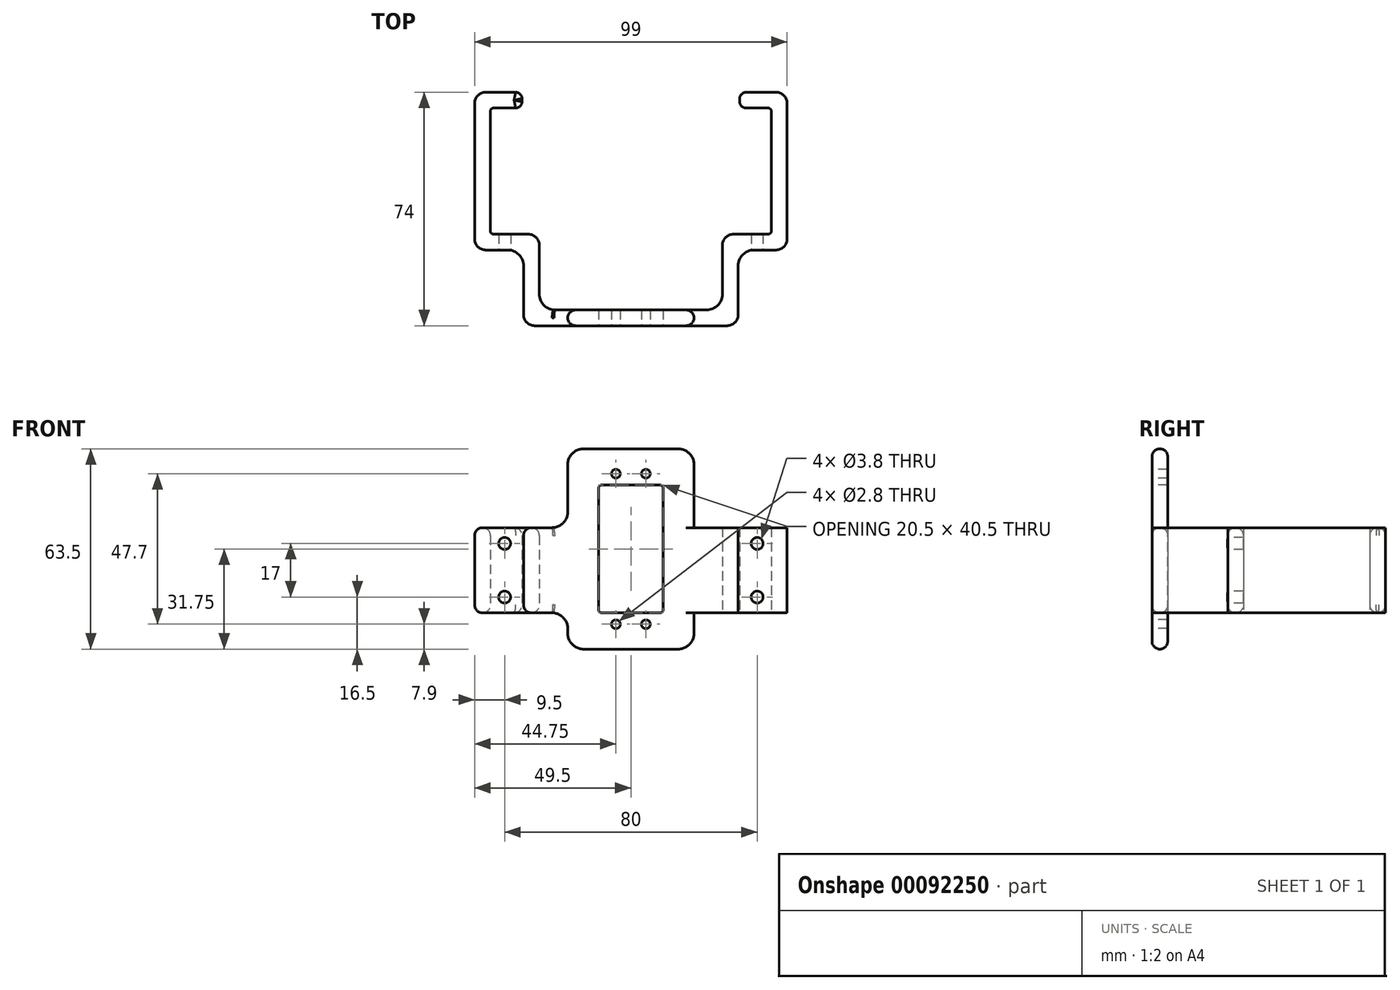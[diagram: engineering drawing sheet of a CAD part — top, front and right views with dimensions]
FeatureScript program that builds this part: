
annotation { "Feature Type Name" : "Feature", "Feature Type Description" : "" }
export const myFeature = defineFeature(function(context is Context, id is Id, definition is map)
    precondition{}
    {
        {
            var Q0;
            Q0=qCreatedBy(makeId("Top.planeOp"),FACE);
            var sketch = newSketch(context, id + "F0", { "sketchPlane" : qUnion([Q0])});
            skLineSegment(sketch, "E0.bottom", {"start": v(-44.5, -20) * mm, "end": v(44.5, -20) * mm, "construction": true});
            skLineSegment(sketch, "E0.top", {"start": v(-44.5, 20) * mm, "end": v(44.5, 20) * mm, "construction": true});
            skLineSegment(sketch, "E0.left", {"start": v(-44.5, -20) * mm, "end": v(-44.5, 20) * mm, "construction": true});
            skLineSegment(sketch, "E0.right", {"start": v(44.5, -20) * mm, "end": v(44.5, 20) * mm, "construction": true});
            skPoint(sketch, "E0.middle", {"position": v(0, 0) * mm});
            skLineSegment(sketch, "E1", {"start": v(-10.3, -35.5) * mm, "end": v(9.7, -35.5) * mm, "construction": true});
            skLineSegment(sketch, "E2", {"start": v(-44.5, 20) * mm, "end": v(-34.5, 20) * mm});
            skLineSegment(sketch, "E3", {"start": v(-34.5, 20) * mm, "end": v(-34.5, 25) * mm});
            skLineSegment(sketch, "E4", {"start": v(-34.5, 25) * mm, "end": v(-49.5, 25) * mm});
            skLineSegment(sketch, "E5", {"start": v(-49.5, 25) * mm, "end": v(-49.5, -25) * mm});
            skLineSegment(sketch, "E6", {"start": v(-49.5, -25) * mm, "end": v(-34, -25) * mm});
            skLineSegment(sketch, "E7", {"start": v(-34, -25) * mm, "end": v(-34, -49) * mm});
            skLineSegment(sketch, "E8", {"start": v(-34, -49) * mm, "end": v(0, -49) * mm});
            skLineSegment(sketch, "E9", {"start": v(-44.5, 20) * mm, "end": v(-44.5, -20) * mm});
            skLineSegment(sketch, "E10", {"start": v(-29, -20) * mm, "end": v(-29, -44) * mm});
            skLineSegment(sketch, "E11", {"start": v(-29, -44) * mm, "end": v(0, -44) * mm});
            skLineSegment(sketch, "E12", {"start": v(-29, -20) * mm, "end": v(-44.5, -20) * mm});
            skLineSegment(sketch, "E13.MirrorCS", {"start": v(29, -44) * mm, "end": v(0, -44) * mm});
            skLineSegment(sketch, "E14.MirrorCS", {"start": v(34, -49) * mm, "end": v(0, -49) * mm});
            skLineSegment(sketch, "E15.MirrorCS", {"start": v(34, -25) * mm, "end": v(34, -49) * mm});
            skLineSegment(sketch, "E16.MirrorCS", {"start": v(49.5, -25) * mm, "end": v(34, -25) * mm});
            skLineSegment(sketch, "E17.MirrorCS", {"start": v(49.5, 25) * mm, "end": v(49.5, -25) * mm});
            skLineSegment(sketch, "E18.MirrorCS", {"start": v(34.5, 25) * mm, "end": v(49.5, 25) * mm});
            skLineSegment(sketch, "E19.MirrorCS", {"start": v(34.5, 20) * mm, "end": v(34.5, 25) * mm});
            skLineSegment(sketch, "E20.MirrorCS", {"start": v(44.5, 20) * mm, "end": v(34.5, 20) * mm});
            skLineSegment(sketch, "E21.MirrorCS", {"start": v(44.5, 20) * mm, "end": v(44.5, -20) * mm});
            skLineSegment(sketch, "E22.MirrorCS", {"start": v(29, -20) * mm, "end": v(29, -44) * mm});
            skLineSegment(sketch, "E23.MirrorCS", {"start": v(29, -20) * mm, "end": v(44.5, -20) * mm});
            skSolve(sketch);
        }
        {
            var Q0;
            Q0 = qSketchRegion(id + "F0", true);
            extrude(context, id + "F1", {"entities" : qUnion([Q0]), "depth" : 27 * mm});
        }
        {
            var Q0;
            Q0=makeQuery(id+"F1.opExtrude","CAP_FACE",FACE,{"disambiguationData":[OSD([sQuery(id+"F0.wireOp",EDGE,"E2"),sQuery(id+"F0.wireOp",EDGE,"E3"),sQuery(id+"F0.wireOp",EDGE,"E4"),sQuery(id+"F0.wireOp",EDGE,"E5"),sQuery(id+"F0.wireOp",EDGE,"E6"),sQuery(id+"F0.wireOp",EDGE,"E7"),sQuery(id+"F0.wireOp",EDGE,"E8"),sQuery(id+"F0.wireOp",EDGE,"E9"),sQuery(id+"F0.wireOp",EDGE,"E10"),sQuery(id+"F0.wireOp",EDGE,"E11"),sQuery(id+"F0.wireOp",EDGE,"E12"),sQuery(id+"F0.wireOp",EDGE,"E13.MirrorCS"),sQuery(id+"F0.wireOp",EDGE,"E14.MirrorCS"),sQuery(id+"F0.wireOp",EDGE,"E15.MirrorCS"),sQuery(id+"F0.wireOp",EDGE,"E16.MirrorCS"),sQuery(id+"F0.wireOp",EDGE,"E17.MirrorCS"),sQuery(id+"F0.wireOp",EDGE,"E18.MirrorCS"),sQuery(id+"F0.wireOp",EDGE,"E19.MirrorCS"),sQuery(id+"F0.wireOp",EDGE,"E20.MirrorCS"),sQuery(id+"F0.wireOp",EDGE,"E21.MirrorCS"),sQuery(id+"F0.wireOp",EDGE,"E22.MirrorCS"),sQuery(id+"F0.wireOp",EDGE,"E23.MirrorCS")])],"isStart":true});
            var sketch = newSketch(context, id + "F2", { "sketchPlane" : qUnion([Q0])});
            skLineSegment(sketch, "E24.bottom", {"start": v(-20, 49) * mm, "end": v(20, 49) * mm});
            skLineSegment(sketch, "E24.top", {"start": v(-20, 44) * mm, "end": v(20, 44) * mm});
            skLineSegment(sketch, "E24.left", {"start": v(-20, 49) * mm, "end": v(-20, 44) * mm});
            skLineSegment(sketch, "E24.right", {"start": v(20, 49) * mm, "end": v(20, 44) * mm});
            skPoint(sketch, "E24.middle", {"position": v(0, 46.5) * mm});
            skSolve(sketch);
        }
        {
            var Q0;
            Q0 = qSketchRegion(id + "F2", true);
            extrude(context, id + "F3", {"entities" : qUnion([Q0]), "operationType" : NewBodyOperationType.ADD, "depth" : 11.5 * mm});
        }
        {
            var Q0;
            Q0=makeQuery(id+"F1.opExtrude","CAP_FACE",FACE,{"disambiguationData":[OSD([sQuery(id+"F0.wireOp",EDGE,"E2"),sQuery(id+"F0.wireOp",EDGE,"E3"),sQuery(id+"F0.wireOp",EDGE,"E4"),sQuery(id+"F0.wireOp",EDGE,"E5"),sQuery(id+"F0.wireOp",EDGE,"E6"),sQuery(id+"F0.wireOp",EDGE,"E7"),sQuery(id+"F0.wireOp",EDGE,"E8"),sQuery(id+"F0.wireOp",EDGE,"E9"),sQuery(id+"F0.wireOp",EDGE,"E10"),sQuery(id+"F0.wireOp",EDGE,"E11"),sQuery(id+"F0.wireOp",EDGE,"E12"),sQuery(id+"F0.wireOp",EDGE,"E13.MirrorCS"),sQuery(id+"F0.wireOp",EDGE,"E14.MirrorCS"),sQuery(id+"F0.wireOp",EDGE,"E15.MirrorCS"),sQuery(id+"F0.wireOp",EDGE,"E16.MirrorCS"),sQuery(id+"F0.wireOp",EDGE,"E17.MirrorCS"),sQuery(id+"F0.wireOp",EDGE,"E18.MirrorCS"),sQuery(id+"F0.wireOp",EDGE,"E19.MirrorCS"),sQuery(id+"F0.wireOp",EDGE,"E20.MirrorCS"),sQuery(id+"F0.wireOp",EDGE,"E21.MirrorCS"),sQuery(id+"F0.wireOp",EDGE,"E22.MirrorCS"),sQuery(id+"F0.wireOp",EDGE,"E23.MirrorCS")])],"isStart":false});
            var sketch = newSketch(context, id + "F4", { "sketchPlane" : qUnion([Q0])});
            skLineSegment(sketch, "E25.bottom", {"start": v(-20, -49) * mm, "end": v(20, -49) * mm});
            skLineSegment(sketch, "E25.top", {"start": v(-20, -44) * mm, "end": v(20, -44) * mm});
            skLineSegment(sketch, "E25.left", {"start": v(-20, -49) * mm, "end": v(-20, -44) * mm});
            skLineSegment(sketch, "E25.right", {"start": v(20, -49) * mm, "end": v(20, -44) * mm});
            skPoint(sketch, "E25.middle", {"position": v(0, -46.5) * mm});
            skPoint(sketch, "E25.middle.positionSnap0", {"position": v(0, -49) * mm});
            skPoint(sketch, "E25.centerSnap0", {"position": v(0, -49) * mm});
            skSolve(sketch);
        }
        {
            var Q0;
            Q0 = qSketchRegion(id + "F4", true);
            extrude(context, id + "F5", {"entities" : qUnion([Q0]), "operationType" : NewBodyOperationType.ADD, "depth" : 25 * mm});
        }
        {
            var Q0;
            Q0=makeQuery(id+"F5.boolean.opBoolean","MERGE",FACE,{"derivedFrom":[makeQuery(id+"F3.boolean.opBoolean","MERGE",FACE,{"derivedFrom":[makeQuery(id+"F1.opExtrude","SWEPT_FACE",FACE,{"disambiguationData":[OSD([sQuery(id+"F0.wireOp",EDGE,"E8"),sQuery(id+"F0.wireOp",EDGE,"E14.MirrorCS")])]}),makeQuery(id+"F3.opExtrude","SWEPT_FACE",FACE,{"disambiguationData":[OSD([sQuery(id+"F2.wireOp",EDGE,"E24.bottom")])]})]}),makeQuery(id+"F5.opExtrude","SWEPT_FACE",FACE,{"disambiguationData":[OSD([sQuery(id+"F4.wireOp",EDGE,"E25.bottom")])]})]});
            var sketch = newSketch(context, id + "F6", { "sketchPlane" : qUnion([Q0])});
            skLineSegment(sketch, "E26.bottom", {"start": v(-10.25, 0) * mm, "end": v(10.25, 0) * mm});
            skLineSegment(sketch, "E26.top", {"start": v(-10.25, 40.5) * mm, "end": v(10.25, 40.5) * mm});
            skLineSegment(sketch, "E26.left", {"start": v(-10.25, 0) * mm, "end": v(-10.25, 40.5) * mm});
            skLineSegment(sketch, "E26.right", {"start": v(10.25, 0) * mm, "end": v(10.25, 40.5) * mm});
            skPoint(sketch, "E26.middle", {"position": v(0, 20.25) * mm});
            skSolve(sketch);
        }
        {
            var Q0;
            Q0 = qSketchRegion(id + "F6", true);
            extrude(context, id + "F7", {"entities" : qUnion([Q0]), "operationType" : NewBodyOperationType.REMOVE, "oppositeDirection" : true, "depth" : 25 * mm});
        }
        {
            var Q0;
            Q0=makeQuery(id+"F1.opExtrude","SWEPT_EDGE",EDGE,{"disambiguationData":[OSD([sQuery(id+"F0.wireOp",EDGE,"E6"),sQuery(id+"F0.wireOp",EDGE,"E7")])]});
            var Q1;
            Q1=makeQuery(id+"F1.opExtrude","SWEPT_EDGE",EDGE,{"disambiguationData":[OSD([sQuery(id+"F0.wireOp",EDGE,"E15.MirrorCS"),sQuery(id+"F0.wireOp",EDGE,"E16.MirrorCS")])]});
            fillet(context, id + "F8", {"entities" : qUnion([Q0, Q1]), "radius" : 5 * mm, "tangentPropagation" : true, "allowEdgeOverflow" : false});
        }
        {
            var Q0;
            Q0=makeQuery(id+"F1.opExtrude","SWEPT_EDGE",EDGE,{"disambiguationData":[OSD([sQuery(id+"F0.wireOp",EDGE,"E10"),sQuery(id+"F0.wireOp",EDGE,"E12")])]});
            var Q1;
            Q1=makeQuery(id+"F1.opExtrude","SWEPT_EDGE",EDGE,{"disambiguationData":[OSD([sQuery(id+"F0.wireOp",EDGE,"E22.MirrorCS"),sQuery(id+"F0.wireOp",EDGE,"E23.MirrorCS")])]});
            var Q2;
            Q2=makeQuery(id+"F1.opExtrude","SWEPT_EDGE",EDGE,{"disambiguationData":[OSD([sQuery(id+"F0.wireOp",EDGE,"E5"),sQuery(id+"F0.wireOp",EDGE,"E6")])]});
            var Q3;
            Q3=makeQuery(id+"F1.opExtrude","SWEPT_EDGE",EDGE,{"disambiguationData":[OSD([sQuery(id+"F0.wireOp",EDGE,"E7"),sQuery(id+"F0.wireOp",EDGE,"E8")])]});
            var Q4;
            Q4=makeQuery(id+"F1.opExtrude","SWEPT_EDGE",EDGE,{"disambiguationData":[OSD([sQuery(id+"F0.wireOp",EDGE,"E14.MirrorCS"),sQuery(id+"F0.wireOp",EDGE,"E15.MirrorCS")])]});
            var Q5;
            Q5=makeQuery(id+"F1.opExtrude","SWEPT_EDGE",EDGE,{"disambiguationData":[OSD([sQuery(id+"F0.wireOp",EDGE,"E16.MirrorCS"),sQuery(id+"F0.wireOp",EDGE,"E17.MirrorCS")])]});
            var Q6;
            Q6=makeQuery(id+"F1.opExtrude","SWEPT_EDGE",EDGE,{"disambiguationData":[OSD([sQuery(id+"F0.wireOp",EDGE,"E4"),sQuery(id+"F0.wireOp",EDGE,"E5")])]});
            var Q7;
            Q7=makeQuery(id+"F1.opExtrude","SWEPT_EDGE",EDGE,{"disambiguationData":[OSD([sQuery(id+"F0.wireOp",EDGE,"E17.MirrorCS"),sQuery(id+"F0.wireOp",EDGE,"E18.MirrorCS")])]});
            fillet(context, id + "F9", {"entities" : qUnion([Q0, Q1, Q2, Q3, Q4, Q5, Q6, Q7]), "radius" : 3.5 * mm, "tangentPropagation" : true, "allowEdgeOverflow" : false});
        }
        {
            var Q0;
            Q0=makeQuery(id+"F1.opExtrude","SWEPT_EDGE",EDGE,{"disambiguationData":[OSD([sQuery(id+"F0.wireOp",EDGE,"E10"),sQuery(id+"F0.wireOp",EDGE,"E11")])]});
            var Q1;
            Q1=makeQuery(id+"F1.opExtrude","SWEPT_EDGE",EDGE,{"disambiguationData":[OSD([sQuery(id+"F0.wireOp",EDGE,"E13.MirrorCS"),sQuery(id+"F0.wireOp",EDGE,"E22.MirrorCS")])]});
            fillet(context, id + "F10", {"entities" : qUnion([Q0, Q1]), "radius" : 5 * mm, "tangentPropagation" : true, "allowEdgeOverflow" : false});
        }
        {
            var Q0;
            Q0=makeQuery(id+"F3.opExtrude","CAP_EDGE",EDGE,{"disambiguationData":[OSD([sQuery(id+"F2.wireOp",EDGE,"E24.left")])],"isStart":true});
            var Q1;
            Q1=makeQuery(id+"F3.opExtrude","CAP_EDGE",EDGE,{"disambiguationData":[OSD([sQuery(id+"F2.wireOp",EDGE,"E24.right")])],"isStart":true});
            var Q2;
            Q2=makeQuery(id+"F3.opExtrude","CAP_EDGE",EDGE,{"disambiguationData":[OSD([sQuery(id+"F2.wireOp",EDGE,"E24.right")])],"isStart":false});
            var Q3;
            Q3=makeQuery(id+"F3.opExtrude","CAP_EDGE",EDGE,{"disambiguationData":[OSD([sQuery(id+"F2.wireOp",EDGE,"E24.left")])],"isStart":false});
            var Q4;
            Q4=makeQuery(id+"F5.opExtrude","CAP_EDGE",EDGE,{"disambiguationData":[OSD([sQuery(id+"F4.wireOp",EDGE,"E25.left")])],"isStart":false});
            var Q5;
            Q5=makeQuery(id+"F5.opExtrude","CAP_EDGE",EDGE,{"disambiguationData":[OSD([sQuery(id+"F4.wireOp",EDGE,"E25.right")])],"isStart":false});
            var Q6;
            Q6=makeQuery(id+"F5.opExtrude","CAP_EDGE",EDGE,{"disambiguationData":[OSD([sQuery(id+"F4.wireOp",EDGE,"E25.right")])],"isStart":true});
            var Q7;
            Q7=makeQuery(id+"F5.opExtrude","CAP_EDGE",EDGE,{"disambiguationData":[OSD([sQuery(id+"F4.wireOp",EDGE,"E25.left")])],"isStart":true});
            fillet(context, id + "F11", {"entities" : qUnion([Q0, Q1, Q2, Q3, Q4, Q5, Q6, Q7]), "radius" : 5 * mm, "tangentPropagation" : true, "allowEdgeOverflow" : false});
        }
        {
            var Q0;
            Q0=makeQuery(id+"F1.opExtrude","SWEPT_EDGE",EDGE,{"disambiguationData":[OSD([sQuery(id+"F0.wireOp",EDGE,"E2"),sQuery(id+"F0.wireOp",EDGE,"E3")])]});
            var Q1;
            Q1=makeQuery(id+"F1.opExtrude","SWEPT_EDGE",EDGE,{"disambiguationData":[OSD([sQuery(id+"F0.wireOp",EDGE,"E18.MirrorCS"),sQuery(id+"F0.wireOp",EDGE,"E19.MirrorCS")])]});
            var Q2;
            Q2=makeQuery(id+"F1.opExtrude","SWEPT_EDGE",EDGE,{"disambiguationData":[OSD([sQuery(id+"F0.wireOp",EDGE,"E19.MirrorCS"),sQuery(id+"F0.wireOp",EDGE,"E20.MirrorCS")])]});
            var Q3;
            Q3=makeQuery(id+"F1.opExtrude","SWEPT_EDGE",EDGE,{"disambiguationData":[OSD([sQuery(id+"F0.wireOp",EDGE,"E3"),sQuery(id+"F0.wireOp",EDGE,"E4")])]});
            fillet(context, id + "F12", {"entities" : qUnion([Q0, Q1, Q2, Q3]), "radius" : 2 * mm, "tangentPropagation" : true, "allowEdgeOverflow" : false});
        }
        {
            var Q0;
            Q0=makeQuery(id+"F1.opExtrude","SWEPT_EDGE",EDGE,{"disambiguationData":[OSD([sQuery(id+"F0.wireOp",EDGE,"E21.MirrorCS"),sQuery(id+"F0.wireOp",EDGE,"E23.MirrorCS")])]});
            var Q1;
            Q1=makeQuery(id+"F1.opExtrude","SWEPT_EDGE",EDGE,{"disambiguationData":[OSD([sQuery(id+"F0.wireOp",EDGE,"E20.MirrorCS"),sQuery(id+"F0.wireOp",EDGE,"E21.MirrorCS")])]});
            var Q2;
            Q2=makeQuery(id+"F1.opExtrude","SWEPT_EDGE",EDGE,{"disambiguationData":[OSD([sQuery(id+"F0.wireOp",EDGE,"E2"),sQuery(id+"F0.wireOp",EDGE,"E9")])]});
            var Q3;
            Q3=makeQuery(id+"F1.opExtrude","SWEPT_EDGE",EDGE,{"disambiguationData":[OSD([sQuery(id+"F0.wireOp",EDGE,"E9"),sQuery(id+"F0.wireOp",EDGE,"E12")])]});
            fillet(context, id + "F13", {"entities" : qUnion([Q0, Q1, Q2, Q3]), "radius" : 1 * mm, "tangentPropagation" : true, "allowEdgeOverflow" : false});
        }
        {
            var Q0;
            Q0=makeQuery(id+"F1.opExtrude","SWEPT_FACE",FACE,{"disambiguationData":[OSD([sQuery(id+"F0.wireOp",EDGE,"E6")])]});
            var sketch = newSketch(context, id + "F14", { "sketchPlane" : qUnion([Q0])});
            skCircle(sketch, "E27", {"center": v(-40, 22) * mm, "radius": 1.9 * mm});
            skCircle(sketch, "E28", {"center": v(-40, 5) * mm, "radius": 1.9 * mm});
            skLineSegment(sketch, "E29", {"start": v(-40, 27) * mm, "end": v(-40, 0) * mm, "construction": true});
            skCircle(sketch, "E30.MirrorC", {"center": v(40, 5) * mm, "radius": 1.9 * mm});
            skCircle(sketch, "E31.MirrorC", {"center": v(40, 22) * mm, "radius": 1.9 * mm});
            skSolve(sketch);
        }
        {
            var Q0;
            Q0 = qSketchRegion(id + "F14", true);
            extrude(context, id + "F15", {"entities" : qUnion([Q0]), "operationType" : NewBodyOperationType.REMOVE, "oppositeDirection" : true, "depth" : 25 * mm, "hasSecondDirection" : true, "secondDirectionOppositeDirection" : false, "secondDirectionDepth" : 25 * mm});
        }
        {
            var Q0;
            Q0=makeQuery(id+"F7.boolean.opBoolean","COPY",EDGE,{"derivedFrom":makeQuery(id+"F7.opExtrude","SWEPT_EDGE",EDGE,{"disambiguationData":[OSD([sQuery(id+"F6.wireOp",EDGE,"E26.top"),sQuery(id+"F6.wireOp",EDGE,"E26.left")])]})});
            var Q1;
            Q1=makeQuery(id+"F7.boolean.opBoolean","COPY",EDGE,{"derivedFrom":makeQuery(id+"F7.opExtrude","SWEPT_EDGE",EDGE,{"disambiguationData":[OSD([sQuery(id+"F6.wireOp",EDGE,"E26.bottom"),sQuery(id+"F6.wireOp",EDGE,"E26.right")])]})});
            var Q2;
            Q2=makeQuery(id+"F7.boolean.opBoolean","COPY",EDGE,{"derivedFrom":makeQuery(id+"F7.opExtrude","SWEPT_EDGE",EDGE,{"disambiguationData":[OSD([sQuery(id+"F6.wireOp",EDGE,"E26.bottom"),sQuery(id+"F6.wireOp",EDGE,"E26.left")])]})});
            var Q3;
            Q3=makeQuery(id+"F7.boolean.opBoolean","COPY",EDGE,{"derivedFrom":makeQuery(id+"F7.opExtrude","SWEPT_EDGE",EDGE,{"disambiguationData":[OSD([sQuery(id+"F6.wireOp",EDGE,"E26.top"),sQuery(id+"F6.wireOp",EDGE,"E26.right")])]})});
            fillet(context, id + "F16", {"entities" : qUnion([Q0, Q1, Q2, Q3]), "radius" : 1 * mm, "tangentPropagation" : true, "allowEdgeOverflow" : false});
        }
        {
            var Q0;
            Q0=makeQuery(id+"F5.boolean.opBoolean","MERGE",FACE,{"derivedFrom":[makeQuery(id+"F3.boolean.opBoolean","MERGE",FACE,{"derivedFrom":[makeQuery(id+"F1.opExtrude","SWEPT_FACE",FACE,{"disambiguationData":[OSD([sQuery(id+"F0.wireOp",EDGE,"E8"),sQuery(id+"F0.wireOp",EDGE,"E14.MirrorCS")])]}),makeQuery(id+"F3.opExtrude","SWEPT_FACE",FACE,{"disambiguationData":[OSD([sQuery(id+"F2.wireOp",EDGE,"E24.bottom")])]})]}),makeQuery(id+"F5.opExtrude","SWEPT_FACE",FACE,{"disambiguationData":[OSD([sQuery(id+"F4.wireOp",EDGE,"E25.bottom")])]})]});
            var sketch = newSketch(context, id + "F17", { "sketchPlane" : qUnion([Q0])});
            skLineSegment(sketch, "E32", {"start": v(-10.25, 20.25) * mm, "end": v(10.25, 20.25) * mm, "construction": true});
            skCircle(sketch, "E33", {"center": v(-4.75, 44.1) * mm, "radius": 1.4 * mm});
            skCircle(sketch, "E34.MirrorC", {"center": v(-4.75, -3.6) * mm, "radius": 1.4 * mm});
            skCircle(sketch, "E35.MirrorC", {"center": v(4.75, -3.6) * mm, "radius": 1.4 * mm});
            skCircle(sketch, "E36.MirrorC", {"center": v(4.75, 44.1) * mm, "radius": 1.4 * mm});
            skSolve(sketch);
        }
        {
            var Q0;
            Q0 = qSketchRegion(id + "F17", true);
            extrude(context, id + "F18", {"entities" : qUnion([Q0]), "operationType" : NewBodyOperationType.REMOVE, "oppositeDirection" : true, "depth" : 25 * mm});
        }
        {
            var Q0;
            {var subQ0=sQuery(id+"F0.wireOp",EDGE,"E13.MirrorCS");var subQ1=sQuery(id+"F0.wireOp",EDGE,"E11");var subQ2=sQuery(id+"F0.wireOp",EDGE,"E9");var subQ3=sQuery(id+"F0.wireOp",EDGE,"E14.MirrorCS");var subQ4=sQuery(id+"F0.wireOp",EDGE,"E8");var subQ5=sQuery(id+"F0.wireOp",EDGE,"E7");var subQ6=sQuery(id+"F0.wireOp",EDGE,"E6");var subQ7=sQuery(id+"F0.wireOp",EDGE,"E2");var subQ8=sQuery(id+"F0.wireOp",EDGE,"E10");var subQ9=sQuery(id+"F0.wireOp",EDGE,"E3");var subQ10=sQuery(id+"F0.wireOp",EDGE,"E4");var subQ11=sQuery(id+"F0.wireOp",EDGE,"E5");var subQ12=sQuery(id+"F0.wireOp",EDGE,"E12");Q0=makeQuery(id+"F5.boolean.opBoolean","SPLIT",FACE,{"disambiguationData":[TD([makeQuery(id+"F1.opExtrude","SWEPT_FACE",FACE,{"disambiguationData":[OSD([subQ7])]})])],"derivedFrom":makeQuery(id+"F1.opExtrude","CAP_FACE",FACE,{"disambiguationData":[OSD([subQ7,subQ9,subQ10,subQ11,subQ6,subQ5,subQ4,subQ2,subQ8,subQ1,subQ12,subQ0,subQ3,sQuery(id+"F0.wireOp",EDGE,"E15.MirrorCS"),sQuery(id+"F0.wireOp",EDGE,"E16.MirrorCS"),sQuery(id+"F0.wireOp",EDGE,"E17.MirrorCS"),sQuery(id+"F0.wireOp",EDGE,"E18.MirrorCS"),sQuery(id+"F0.wireOp",EDGE,"E19.MirrorCS"),sQuery(id+"F0.wireOp",EDGE,"E20.MirrorCS"),sQuery(id+"F0.wireOp",EDGE,"E21.MirrorCS"),sQuery(id+"F0.wireOp",EDGE,"E22.MirrorCS"),sQuery(id+"F0.wireOp",EDGE,"E23.MirrorCS")])],"isStart":false})});}
            fillet(context, id + "F19", {"entities" : qUnion([Q0]), "radius" : 2.5 * mm, "tangentPropagation" : true, "allowEdgeOverflow" : false});
        }
        {
            var Q0;
            {var subQ0=sQuery(id+"F0.wireOp",EDGE,"E13.MirrorCS");var subQ1=sQuery(id+"F0.wireOp",EDGE,"E11");var subQ2=sQuery(id+"F0.wireOp",EDGE,"E9");var subQ3=sQuery(id+"F0.wireOp",EDGE,"E14.MirrorCS");var subQ4=sQuery(id+"F0.wireOp",EDGE,"E8");var subQ5=sQuery(id+"F0.wireOp",EDGE,"E7");var subQ6=sQuery(id+"F0.wireOp",EDGE,"E6");var subQ7=sQuery(id+"F0.wireOp",EDGE,"E2");var subQ8=sQuery(id+"F0.wireOp",EDGE,"E10");var subQ9=sQuery(id+"F0.wireOp",EDGE,"E3");var subQ10=sQuery(id+"F0.wireOp",EDGE,"E4");var subQ11=sQuery(id+"F0.wireOp",EDGE,"E5");var subQ12=sQuery(id+"F0.wireOp",EDGE,"E12");Q0=makeQuery(id+"F3.boolean.opBoolean","SPLIT",FACE,{"disambiguationData":[TD([makeQuery(id+"F1.opExtrude","SWEPT_FACE",FACE,{"disambiguationData":[OSD([subQ7])]})])],"derivedFrom":makeQuery(id+"F1.opExtrude","CAP_FACE",FACE,{"disambiguationData":[OSD([subQ7,subQ9,subQ10,subQ11,subQ6,subQ5,subQ4,subQ2,subQ8,subQ1,subQ12,subQ0,subQ3,sQuery(id+"F0.wireOp",EDGE,"E15.MirrorCS"),sQuery(id+"F0.wireOp",EDGE,"E16.MirrorCS"),sQuery(id+"F0.wireOp",EDGE,"E17.MirrorCS"),sQuery(id+"F0.wireOp",EDGE,"E18.MirrorCS"),sQuery(id+"F0.wireOp",EDGE,"E19.MirrorCS"),sQuery(id+"F0.wireOp",EDGE,"E20.MirrorCS"),sQuery(id+"F0.wireOp",EDGE,"E21.MirrorCS"),sQuery(id+"F0.wireOp",EDGE,"E22.MirrorCS"),sQuery(id+"F0.wireOp",EDGE,"E23.MirrorCS")])],"isStart":true})});}
            fillet(context, id + "F20", {"entities" : qUnion([Q0]), "radius" : 2.5 * mm, "tangentPropagation" : true, "allowEdgeOverflow" : false});
        }
    });
